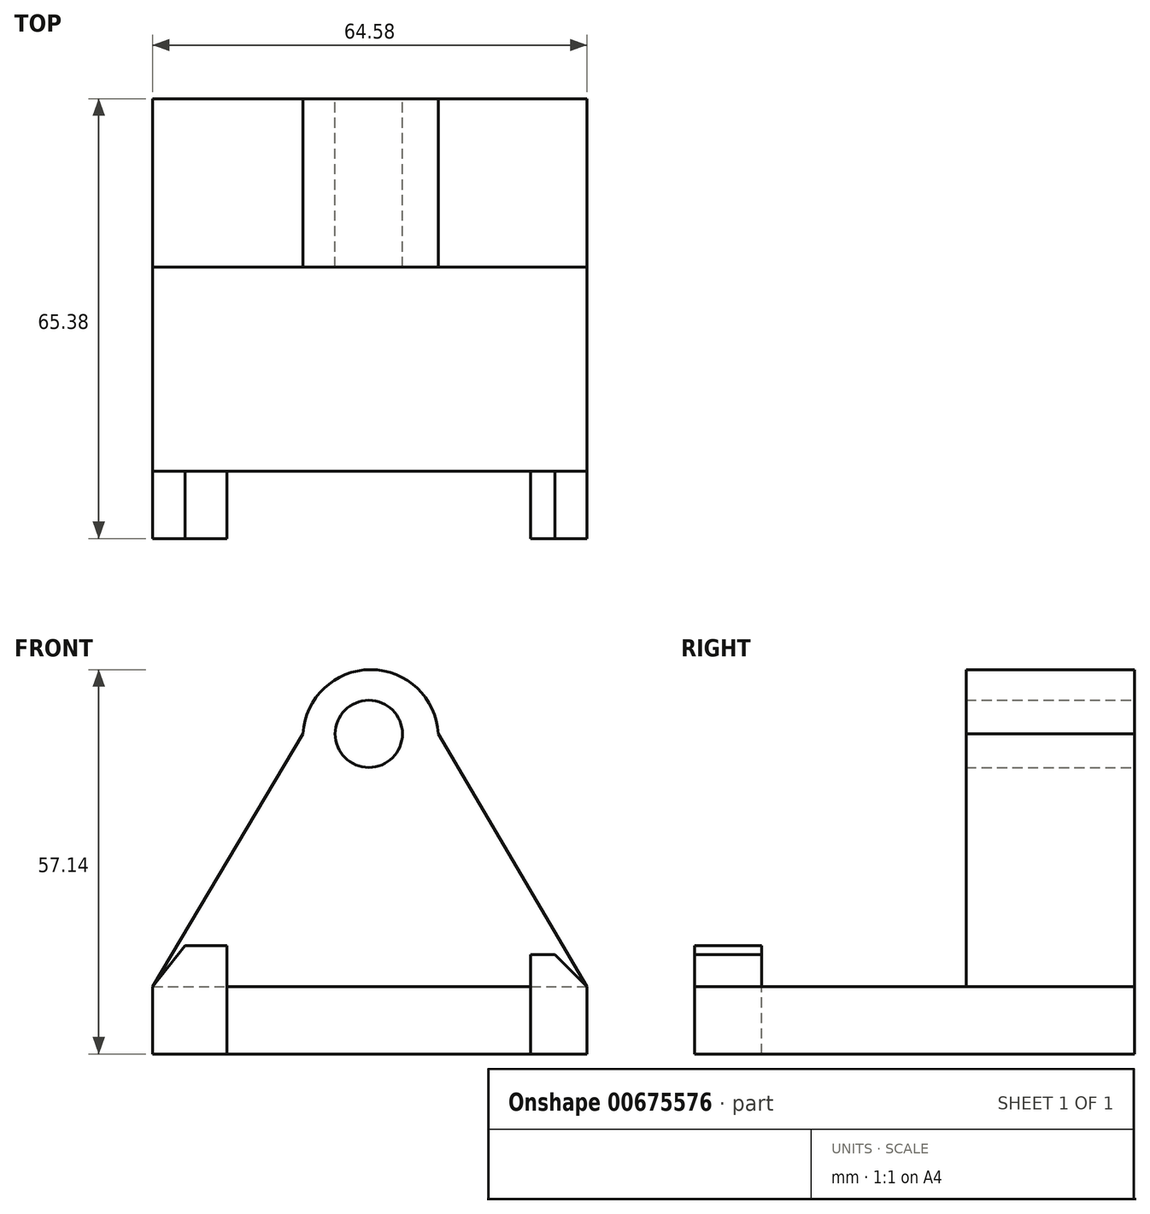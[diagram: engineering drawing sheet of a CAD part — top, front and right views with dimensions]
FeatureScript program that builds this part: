
annotation { "Feature Type Name" : "Feature", "Feature Type Description" : "" }
export const myFeature = defineFeature(function(context is Context, id is Id, definition is map)
    precondition{}
    {
        {
            var Q0;
            Q0=qCreatedBy(makeId("Front.planeOp"),FACE);
            var sketch = newSketch(context, id + "F0", { "sketchPlane" : qUnion([Q0])});
            skCircle(sketch, "E0", {"center": v(0, 37.6) * mm, "radius": 5 * mm});
            skArc(sketch, "E1", {"start": v(10.34, 37.6) * mm, "mid": v(0.28, 47.14) * mm, "end": v(-9.77, 37.6) * mm});
            skLineSegment(sketch, "E2", {"start": v(-9.77, 37.6) * mm, "end": v(-32.15, 0) * mm});
            skLineSegment(sketch, "E3", {"start": v(10.34, 37.6) * mm, "end": v(32.43, 0) * mm});
            skLineSegment(sketch, "E4", {"start": v(32.43, 0) * mm, "end": v(-32.15, 0) * mm});
            skSolve(sketch);
        }
        {
            var Q0;
            Q0 = qSketchRegion(id + "F0", true);
            extrude(context, id + "F1", {"entities" : qUnion([Q0]), "depth" : 25 * mm, "offsetDistance" : 25 * mm});
        }
        {
            var Q0;
            Q0=makeQuery(id+"F1.opExtrude","SWEPT_FACE",FACE,{"disambiguationData":[OSD([sQuery(id+"F0.wireOp",EDGE,"E4")])]});
            var sketch = newSketch(context, id + "F2", { "sketchPlane" : qUnion([Q0])});
            skLineSegment(sketch, "E5", {"start": v(-32.15, 0) * mm, "end": v(-32.15, 55.38) * mm});
            skLineSegment(sketch, "E6", {"start": v(-32.15, 55.38) * mm, "end": v(32.43, 55.38) * mm});
            skLineSegment(sketch, "E7", {"start": v(32.43, 55.38) * mm, "end": v(32.43, 0) * mm});
            skSolve(sketch);
        }
        {
            var Q0;
            {var subQ2=sQuery(id+"F2.wireOp",EDGE,"E6");Q0=makeQuery(id+"F2.imprint","IMPRINT",FACE,{"disambiguationData":[TD([[makeQuery(id+"F2.imprint","IMPRINT",EDGE,{"derivedFrom":subQ2}),-1.0]])]});}
            var Q1;
            {var subQ1=sQuery(id+"F0.wireOp",EDGE,"E4");var subQ2=makeQuery(id+"F1.opExtrude","CAP_EDGE",EDGE,{"disambiguationData":[OSD([subQ1])],"isStart":true});Q1=makeQuery(id+"F2.imprint","IMPRINT",FACE,{"disambiguationData":[TD([[makeQuery(id+"F2.imprint","IMPRINT",EDGE,{"derivedFrom":subQ2}),-1.0]])]});}
            extrude(context, id + "F3", {"entities" : qUnion([Q0, Q1]), "operationType" : NewBodyOperationType.ADD, "depth" : 10 * mm, "offsetDistance" : 25 * mm});
        }
        {
            var Q0;
            Q0=makeQuery(id+"F3.opExtrude","SWEPT_FACE",FACE,{"disambiguationData":[OSD([sQuery(id+"F2.wireOp",EDGE,"E6")])]});
            var sketch = newSketch(context, id + "F4", { "sketchPlane" : qUnion([Q0])});
            skLineSegment(sketch, "E8", {"start": v(-32.15, -10) * mm, "end": v(-21.09, -10) * mm});
            skLineSegment(sketch, "E9", {"start": v(-21.09, -10) * mm, "end": v(-21.09, 6.13) * mm});
            skLineSegment(sketch, "E10", {"start": v(-21.09, 6.13) * mm, "end": v(-27.31, 6.13) * mm});
            skLineSegment(sketch, "E11", {"start": v(-27.31, 6.13) * mm, "end": v(-32.15, 0) * mm});
            skLineSegment(sketch, "E12", {"start": v(-32.15, 0) * mm, "end": v(-32.15, -10) * mm});
            skLineSegment(sketch, "E13", {"start": v(32.43, -10) * mm, "end": v(24.07, -10) * mm});
            skLineSegment(sketch, "E14", {"start": v(24.07, -10) * mm, "end": v(24.07, 4.77) * mm});
            skLineSegment(sketch, "E15", {"start": v(24.07, 4.77) * mm, "end": v(27.68, 4.77) * mm});
            skLineSegment(sketch, "E16", {"start": v(27.68, 4.77) * mm, "end": v(32.43, 0) * mm});
            skLineSegment(sketch, "E17", {"start": v(32.43, 0) * mm, "end": v(32.43, -10) * mm});
            skSolve(sketch);
        }
        {
            var Q0;
            Q0 = qSketchRegion(id + "F4", true);
            extrude(context, id + "F5", {"entities" : qUnion([Q0]), "operationType" : NewBodyOperationType.ADD, "depth" : 10 * mm, "offsetDistance" : 25 * mm});
        }
    });
